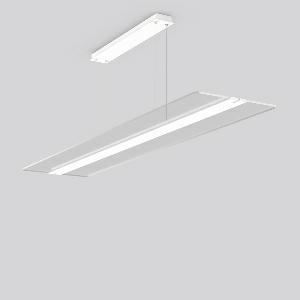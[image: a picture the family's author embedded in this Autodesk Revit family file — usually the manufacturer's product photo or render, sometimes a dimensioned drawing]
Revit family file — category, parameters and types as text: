
# Revit family: twindot_s_312265_002_a9e1
name_source: partatom
category: Lighting Fixtures
units: mm (PartAtom-declared; Revit-internal decimal feet)

## family parameters
Cut with Voids When Loaded = No
Host = Face
Light Source = No
Part Type = Normal
Room Calculation Point = No
Round Connector Dimension = Use Diameter
Shared = No

## types (1)
- TWINDOT S (1 x LED Modul 830, 8100 lm, 3000)
    Apparent Load = 65 VA
    CIE Flux Codes = 47 77 94 55 100
    Color Rendering = 80
    Color Temperature = 3000
    Default Elevation = 1800 mm
    Description = Series: TWINDOT S
LED pendant luminaire with extremely flat and frameless appearance. Middle bar made of aluminium extrusion profile, powder-coated. Transparent light guide made of UV-resistant acrylic glass (PMMA) with TWINDOT prismatic. Light control with perfectly glare-free TWINDOT technology for pleasantly gentle light with soft shadows. Even and wide indirect and direct light distribution. Direct 55%, indirect 45% light emission. 4-point steel cable suspension, steplessly adjustable. Converter integrated in the canopy (powder-coated white). Power supply through suspension cable. 
Colour: traffic white, matt (RAL 9016)
Length: 1500 mm
Width: 350 mm
Height: 20 mm
Suspension length: 500-1200 mm
Lamp: LED
Socket: without socket
Colour temperature: 3000K
Colour rendering index (CRI): 80
System power: 65 W
Rated luminous flux: 8100 lm
Luminous efficiency: 125 lm/W
Control gear: Regulated power supply
Protection class: I
Type of protection: IP 20
    Height = 20 mm  [stored 0.0656168 ft]
    Lamp = 1 x LED Modul 830
    Lamp Light Flux = 8100 lm
    Lamp count = 1
    Length = 1500 mm
    Lifetime = 50000 h
    Luminous efficacy = 125 lm/W
    Manufacturer = RZB
    ModVariant = No
    Model = 312265.002
    Mounting Place = Ceiling
    Mounting Type = Pendant
    Number of Poles = 1
    OnlyDefault = Yes
    Power Factor = 1
    Product Name = TWINDOT S
    Product group = Pendant modular luminaires
    ProductGroupID = 906
    Protection Class = Protection class I
    Protection Degree = IP 20
    RLX_Detail_Level = 1
    RLX_Emergency_Light_Flux = 0 lm
    RLX_Emergency_Type = 0
    RLX_Emergency_Type_DB = No
    RlxData = <blob elided: 36701 chars, md5=44b034fa>
    Socket = socket
    Standby Power = 0 W
    System Light Flux = 8100 lm
    System Power = 65 W
    Type Comments = Product without accessories
    Type Image = 312265.002.jpg
    URL = http://relux.com
    VarID = ---
    Voltage = 230 V
    Voltage Range = 220-240 V
    Weight = 0.00 kg
    Width = 350 mm

note: [stored X ft] marks values corroborated as IEEE doubles in the binary element streams (Revit-internal decimal feet)

## geometry (parser evidence)
native form markers: Blend x4, Sweep x13
no freeform markers — native parametric forms only
